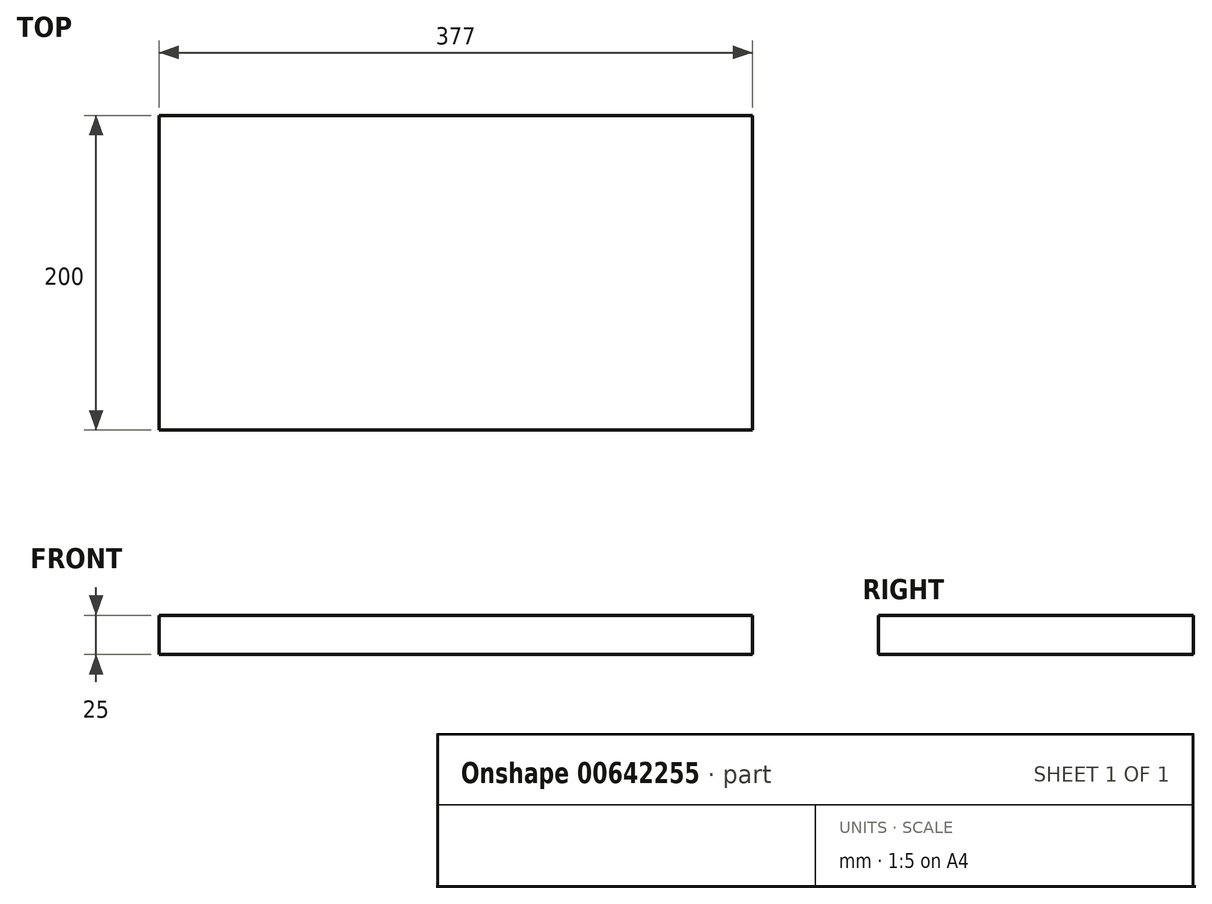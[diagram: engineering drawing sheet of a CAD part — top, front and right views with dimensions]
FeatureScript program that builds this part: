
annotation { "Feature Type Name" : "Feature", "Feature Type Description" : "" }
export const myFeature = defineFeature(function(context is Context, id is Id, definition is map)
    precondition{}
    {
        {
            var Q0;
            Q0=qCreatedBy(makeId("Top.planeOp"),FACE);
            var sketch = newSketch(context, id + "F0", { "sketchPlane" : qUnion([Q0])});
            skLineSegment(sketch, "E0.bottom", {"start": v(-188.5, 100) * mm, "end": v(188.5, 100) * mm});
            skLineSegment(sketch, "E0.top", {"start": v(-188.5, -100) * mm, "end": v(188.5, -100) * mm});
            skLineSegment(sketch, "E0.left", {"start": v(-188.5, 100) * mm, "end": v(-188.5, -100) * mm});
            skLineSegment(sketch, "E0.right", {"start": v(188.5, 100) * mm, "end": v(188.5, -100) * mm});
            skLineSegment(sketch, "E1", {"start": v(0, 100) * mm, "end": v(0, -100) * mm, "construction": true});
            skSolve(sketch);
        }
        {
            var Q0;
            Q0 = qSketchRegion(id + "F0", true);
            var Q1;
            Q1 = qBodyType(qCreatedBy(id + "F0" ,EDGE), BodyType.WIRE);
            var Q2;
            Q2=sQuery(id+"F0.wireOp",EDGE,"E0.right");
            extrude(context, id + "F1", {"entities" : qUnion([Q0]), "surfaceEntities" : qUnion([Q1, Q2]), "depth" : 25 * mm, "offsetDistance" : 25 * mm});
        }
    });
